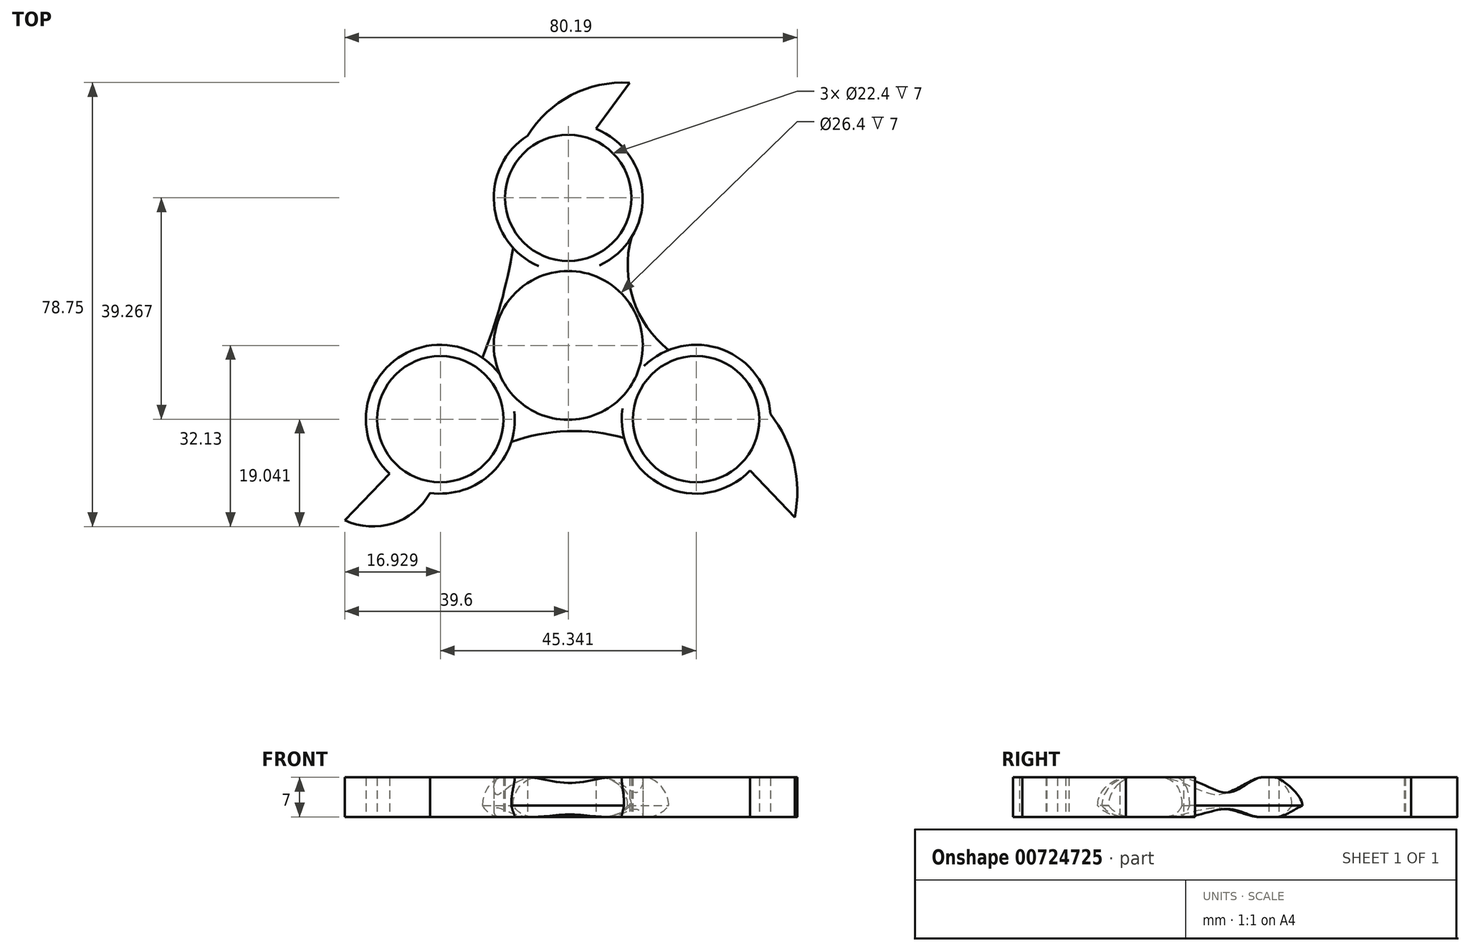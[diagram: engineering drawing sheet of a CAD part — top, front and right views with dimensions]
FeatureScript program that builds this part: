
annotation { "Feature Type Name" : "Feature", "Feature Type Description" : "" }
export const myFeature = defineFeature(function(context is Context, id is Id, definition is map)
    precondition{}
    {
        {
            var Q0;
            Q0=qCreatedBy(makeId("Top.planeOp"),FACE);
            var sketch = newSketch(context, id + "F0", { "sketchPlane" : qUnion([Q0])});
            skCircle(sketch, "E0", {"center": v(0, 0) * mm, "radius": 11.2 * mm});
            skCircle(sketch, "E1", {"center": v(0, 0) * mm, "radius": 13.2 * mm});
            skCircle(sketch, "E2", {"center": v(0, 26.18) * mm, "radius": 13.2 * mm});
            skCircle(sketch, "E3", {"center": v(0, 26.18) * mm, "radius": 11.2 * mm});
            skCircle(sketch, "E4.1.0", {"center": v(-22.67, -13.09) * mm, "radius": 13.2 * mm});
            skCircle(sketch, "E4.1.1", {"center": v(-22.67, -13.09) * mm, "radius": 11.2 * mm});
            skCircle(sketch, "E4.2.0", {"center": v(22.67, -13.09) * mm, "radius": 13.2 * mm});
            skCircle(sketch, "E4.2.1", {"center": v(22.67, -13.09) * mm, "radius": 11.2 * mm});
            skArc(sketch, "E5", {"start": v(-15.21, -2.2) * mm, "mid": v(-11.96, 7.4) * mm, "end": v(-9.78, 17.31) * mm});
            skArc(sketch, "E6", {"start": v(11.2, 19.18) * mm, "mid": v(11.5, 8.19) * mm, "end": v(17.8, -0.82) * mm});
            skArc(sketch, "E7", {"start": v(9.9, -16.4) * mm, "mid": v(-0.16, -15.22) * mm, "end": v(-10.1, -17.13) * mm});
            skArc(sketch, "E8", {"start": v(10.87, 46.58) * mm, "mid": v(0.52, 44.4) * mm, "end": v(-7.24, 37.21) * mm});
            skLineSegment(sketch, "E9", {"start": v(10.87, 46.58) * mm, "end": v(4.9, 38.43) * mm});
            skArc(sketch, "E10", {"start": v(40.14, -30.47) * mm, "mid": v(40, -20.84) * mm, "end": v(35.84, -12.15) * mm});
            skLineSegment(sketch, "E11", {"start": v(32.2, -22.21) * mm, "end": v(40.14, -30.47) * mm});
            skArc(sketch, "E12", {"start": v(-39.6, -31.01) * mm, "mid": v(-31.1, -31.57) * mm, "end": v(-24.51, -26.16) * mm});
            skPoint(sketch, "E13.startSnap0", {"position": v(-31.1, -31.57) * mm});
            skLineSegment(sketch, "E14", {"start": v(-31.64, -22.78) * mm, "end": v(-39.6, -31.01) * mm});
            skSolve(sketch);
        }
        {
            var Q0;
            Q0 = qSketchRegion(id + "F0", true);
            extrude(context, id + "F1", {"entities" : qUnion([Q0]), "depth" : 7 * mm, "offsetDistance" : 25 * mm});
        }
        {
            var Q0;
            Q0=makeQuery(id+"F1.opExtrude","CAP_EDGE",EDGE,{"disambiguationData":[OSD([sQuery(id+"F0.wireOp",EDGE,"E5")])],"isStart":false});
            var Q1;
            Q1=makeQuery(id+"F1.opExtrude","CAP_EDGE",EDGE,{"disambiguationData":[OSD([sQuery(id+"F0.wireOp",EDGE,"E6")])],"isStart":false});
            var Q2;
            Q2=makeQuery(id+"F1.opExtrude","CAP_EDGE",EDGE,{"disambiguationData":[OSD([sQuery(id+"F0.wireOp",EDGE,"E7")])],"isStart":false});
            fillet(context, id + "F2", {"entities" : qUnion([Q0, Q1, Q2]), "radius" : 5 * mm, "tangentPropagation" : true, "allowEdgeOverflow" : false});
        }
        {
            var Q0;
            Q0=makeQuery(id+"F1.opExtrude","CAP_EDGE",EDGE,{"disambiguationData":[OSD([sQuery(id+"F0.wireOp",EDGE,"E6")])],"isStart":true});
            var Q1;
            Q1=makeQuery(id+"F1.opExtrude","CAP_EDGE",EDGE,{"disambiguationData":[OSD([sQuery(id+"F0.wireOp",EDGE,"E7")])],"isStart":true});
            var Q2;
            Q2=makeQuery(id+"F1.opExtrude","CAP_EDGE",EDGE,{"disambiguationData":[OSD([sQuery(id+"F0.wireOp",EDGE,"E5")])],"isStart":true});
            fillet(context, id + "F3", {"entities" : qUnion([Q0, Q1, Q2]), "radius" : 5 * mm, "tangentPropagation" : true, "allowEdgeOverflow" : false});
        }
    });
